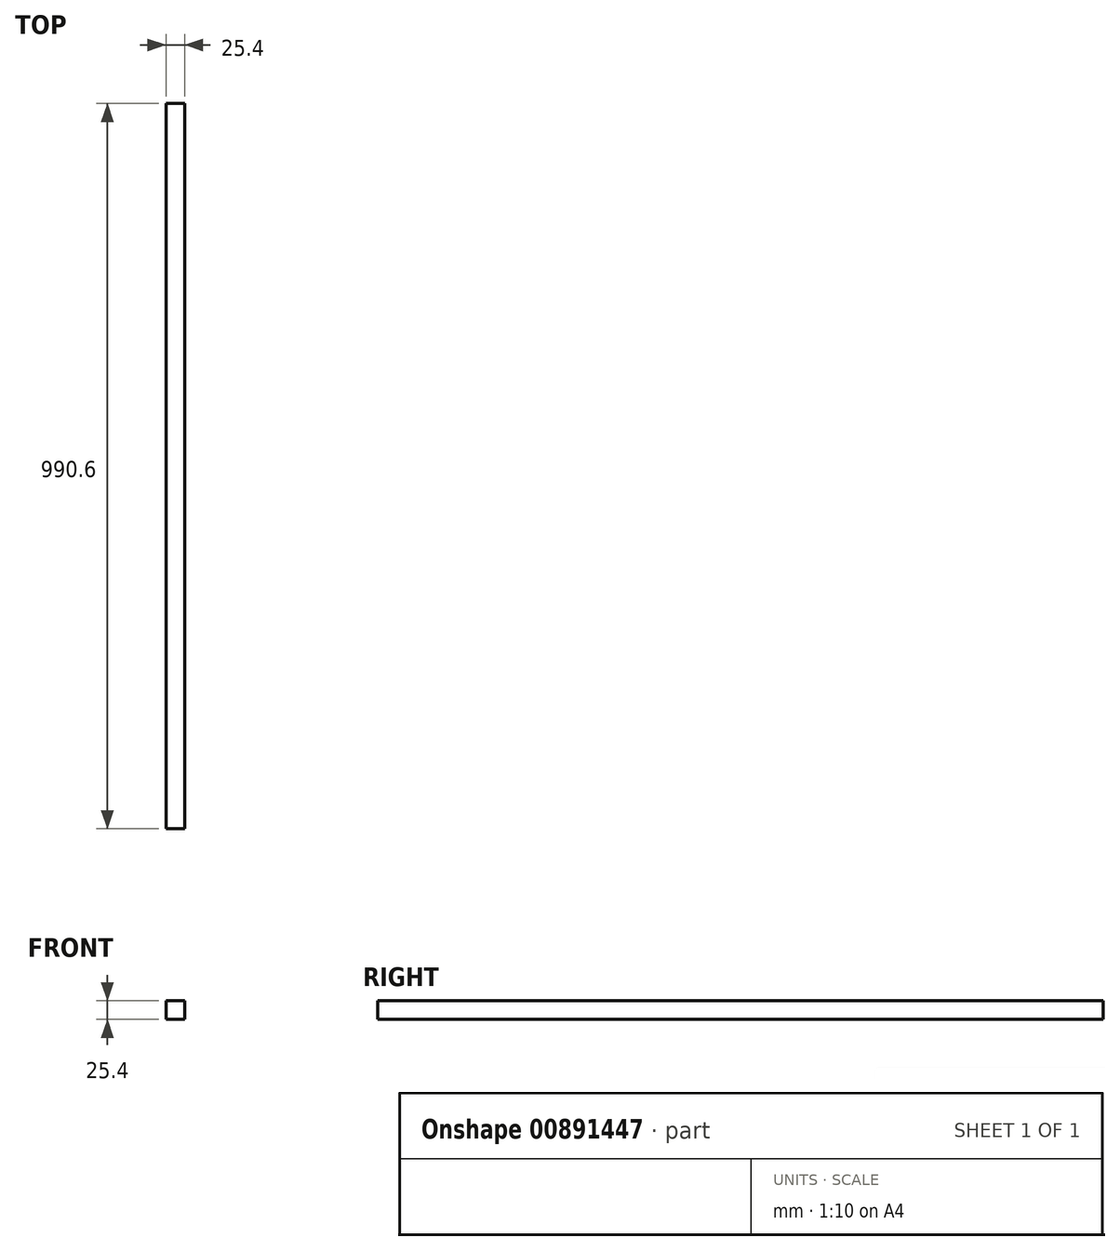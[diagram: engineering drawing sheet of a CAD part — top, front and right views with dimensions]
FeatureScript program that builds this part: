
annotation { "Feature Type Name" : "Feature", "Feature Type Description" : "" }
export const myFeature = defineFeature(function(context is Context, id is Id, definition is map)
    precondition{}
    {
        {
            var Q0;
            Q0=qCreatedBy(makeId("Front.planeOp"),FACE);
            var sketch = newSketch(context, id + "F0", { "sketchPlane" : qUnion([Q0])});
            skLineSegment(sketch, "E0.bottom", {"start": v(-118.89, 30.91) * mm, "end": v(-93.49, 30.91) * mm});
            skLineSegment(sketch, "E0.top", {"start": v(-118.89, 5.51) * mm, "end": v(-93.49, 5.51) * mm});
            skLineSegment(sketch, "E0.left", {"start": v(-118.89, 30.91) * mm, "end": v(-118.89, 5.51) * mm});
            skLineSegment(sketch, "E0.right", {"start": v(-93.49, 30.91) * mm, "end": v(-93.49, 5.51) * mm});
            skSolve(sketch);
        }
        {
            var Q0;
            Q0=makeQuery(id+"F0.imprint","IMPRINT",FACE,{"disambiguationData":[TD([[makeQuery(id+"F0.imprint","IMPRINT",EDGE,{"derivedFrom":sQuery(id+"F0.wireOp",EDGE,"E0.bottom")}),-1.0]])]});
            extrude(context, id + "F1", {"entities" : qUnion([Q0]), "depth" : 990.6 * mm, "offsetDistance" : 25.4 * mm});
        }
    });
